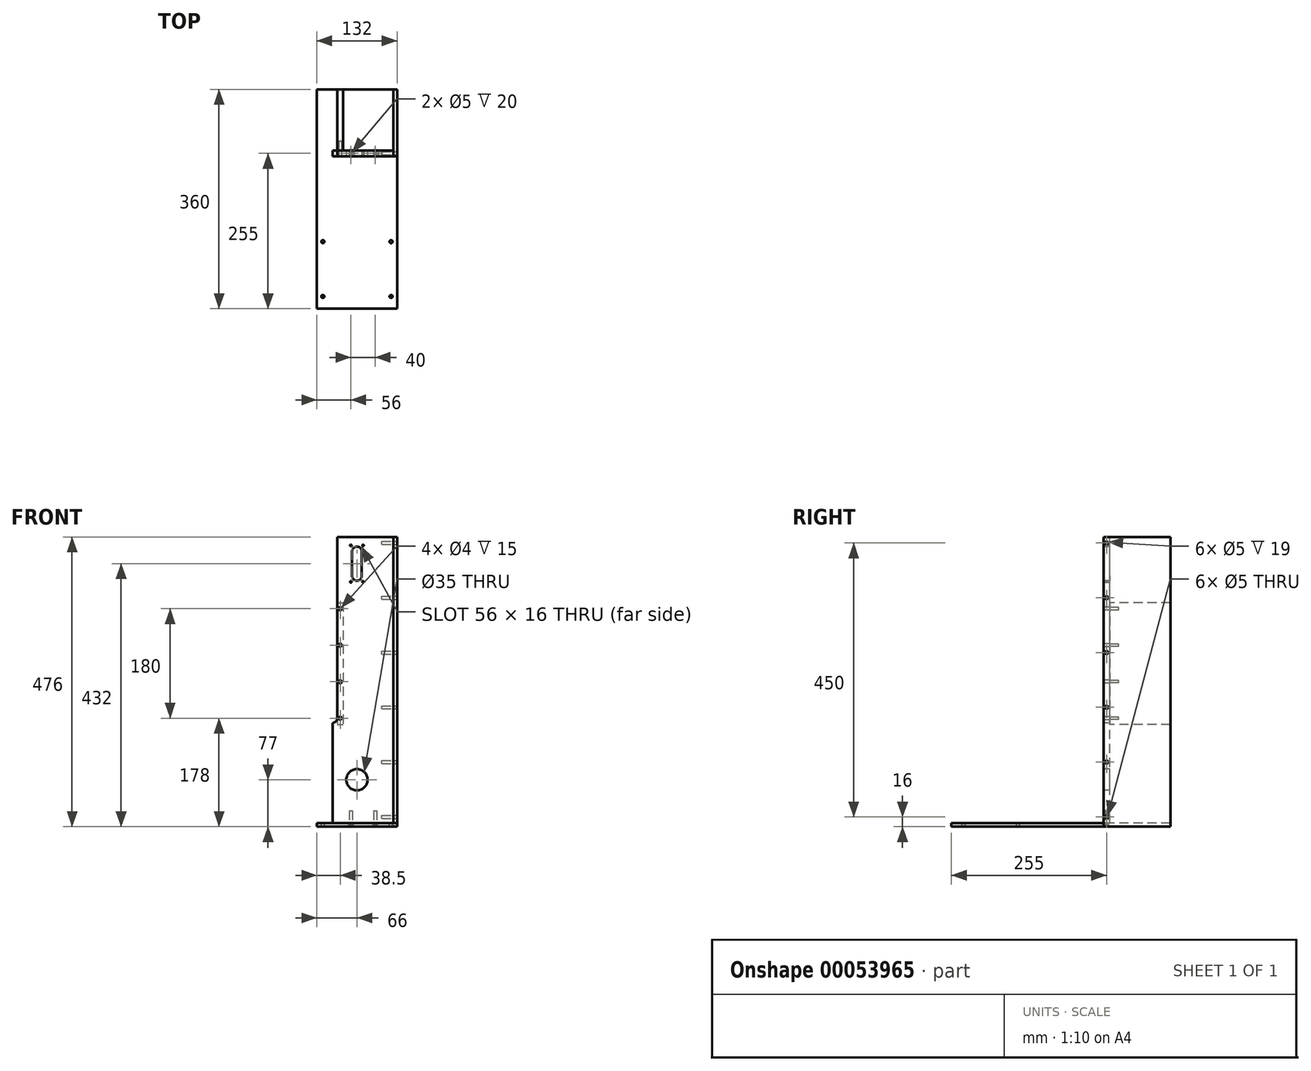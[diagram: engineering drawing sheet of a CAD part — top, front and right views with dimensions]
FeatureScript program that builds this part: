
annotation { "Feature Type Name" : "Feature", "Feature Type Description" : "" }
export const myFeature = defineFeature(function(context is Context, id is Id, definition is map)
    precondition{}
    {
        {
            var Q0;
            Q0=qCreatedBy(makeId("Front.planeOp"),FACE);
            var sketch = newSketch(context, id + "F0", { "sketchPlane" : qUnion([Q0])});
            skLineSegment(sketch, "E0.rect.bottom", {"start": v(50, -235) * mm, "end": v(-50, -235) * mm});
            skLineSegment(sketch, "E0.rect.top", {"start": v(50, 235) * mm, "end": v(-50, 235) * mm});
            skLineSegment(sketch, "E0.rect.left", {"start": v(50, -235) * mm, "end": v(50, 235) * mm});
            skLineSegment(sketch, "E0.rect.right", {"start": v(-50, -235) * mm, "end": v(-50, 235) * mm});
            skPoint(sketch, "E0.rect.middle", {"position": v(0, 0) * mm});
            skSolve(sketch);
        }
        {
            var Q0;
            Q0 = qSketchRegion(id + "F0", true);
            extrude(context, id + "F1", {"entities" : qUnion([Q0]), "depth" : 10 * mm});
        }
        {
            var Q0;
            Q0=makeQuery(id+"F1.opExtrude","CAP_FACE",FACE,{"disambiguationData":[OSD([sQuery(id+"F0.wireOp",EDGE,"E0.rect.bottom"),sQuery(id+"F0.wireOp",EDGE,"E0.rect.top"),sQuery(id+"F0.wireOp",EDGE,"E0.rect.left"),sQuery(id+"F0.wireOp",EDGE,"E0.rect.right")])],"isStart":false});
            var sketch = newSketch(context, id + "F2", { "sketchPlane" : qUnion([Q0])});
            skLineSegment(sketch, "E1", {"start": v(-10, -235) * mm, "end": v(-10, 235) * mm, "construction": true});
            skPoint(sketch, "E2", {"position": v(-10, -164) * mm});
            skPoint(sketch, "E3", {"position": v(-10, 191) * mm});
            skCircle(sketch, "E4", {"center": v(-10, -164) * mm, "radius": 17.5 * mm});
            skLineSegment(sketch, "E5.rect.bottom", {"start": v(-18, 171) * mm, "end": v(-2, 171) * mm});
            skLineSegment(sketch, "E5.rect.top", {"start": v(-18, 211) * mm, "end": v(-2, 211) * mm});
            skLineSegment(sketch, "E5.rect.left", {"start": v(-18, 171) * mm, "end": v(-18, 211) * mm});
            skLineSegment(sketch, "E5.rect.right", {"start": v(-2, 171) * mm, "end": v(-2, 211) * mm});
            skArc(sketch, "E6", {"start": v(-2, 211) * mm, "mid": v(-10, 219) * mm, "end": v(-18, 211) * mm});
            skArc(sketch, "E7", {"start": v(-18, 171) * mm, "mid": v(-10, 163) * mm, "end": v(-2, 171) * mm});
            skLineSegment(sketch, "E8", {"start": v(-10, -164) * mm, "end": v(50, -164) * mm, "construction": true});
            skLineSegment(sketch, "E9", {"start": v(0, 221) * mm, "end": v(0, 191) * mm, "construction": true});
            skCircle(sketch, "E10", {"center": v(0, 221) * mm, "radius": 1.25 * mm});
            skLineSegment(sketch, "E11", {"start": v(-50, 191) * mm, "end": v(50, 191) * mm, "construction": true});
            skPoint(sketch, "E11.startSnap0", {"position": v(-18, 191) * mm});
            skCircle(sketch, "E12.MirrorC", {"center": v(0, 161) * mm, "radius": 1.25 * mm});
            skCircle(sketch, "E13.MirrorC", {"center": v(-20, 221) * mm, "radius": 1.25 * mm});
            skCircle(sketch, "E14.MirrorC", {"center": v(-20, 161) * mm, "radius": 1.25 * mm});
            skSolve(sketch);
        }
        {
            var Q0;
            Q0 = qSketchRegion(id + "F2", true);
            extrude(context, id + "F3", {"entities" : qUnion([Q0]), "operationType" : NewBodyOperationType.REMOVE, "oppositeDirection" : true, "depth" : 25 * mm});
        }
        {
            var Q0;
            Q0=makeQuery(id+"F1.opExtrude","CAP_FACE",FACE,{"disambiguationData":[OSD([sQuery(id+"F0.wireOp",EDGE,"E0.rect.bottom"),sQuery(id+"F0.wireOp",EDGE,"E0.rect.top"),sQuery(id+"F0.wireOp",EDGE,"E0.rect.left"),sQuery(id+"F0.wireOp",EDGE,"E0.rect.right")])],"isStart":false});
            var sketch = newSketch(context, id + "F4", { "sketchPlane" : qUnion([Q0])});
            skPoint(sketch, "E15", {"position": v(-10, -63) * mm});
            skLineSegment(sketch, "E16", {"start": v(22.5, -63) * mm, "end": v(-42.5, -63) * mm, "construction": true});
            skLineSegment(sketch, "E17", {"start": v(-42.5, -63) * mm, "end": v(-42.5, 235) * mm});
            skLineSegment(sketch, "E18", {"start": v(-42.5, -63) * mm, "end": v(-50, -63) * mm, "construction": true});
            skArc(sketch, "E19", {"start": v(-42.5, -63) * mm, "mid": v(-44.7, -68.3) * mm, "end": v(-50, -70.5) * mm});
            skLineSegment(sketch, "E20", {"start": v(-10, 211) * mm, "end": v(-10, -164) * mm, "construction": true});
            skSolve(sketch);
        }
        {
            var Q0;
            Q0 = qSketchRegion(id + "F4", true);
            var Q1;
            {var subQ0=sQuery(id+"F4.wireOp",EDGE,"E17");Q1=makeQuery(id+"F4.imprint","IMPRINT",FACE,{"disambiguationData":[TD([[makeQuery(id+"F4.imprint","IMPRINT",EDGE,{"derivedFrom":subQ0}),1.0]])]});}
            extrude(context, id + "F5", {"entities" : qUnion([Q0, Q1]), "operationType" : NewBodyOperationType.REMOVE, "oppositeDirection" : true, "depth" : 25 * mm});
        }
        {
            var Q0;
            Q0=makeQuery(id+"F1.opExtrude","CAP_FACE",FACE,{"disambiguationData":[OSD([sQuery(id+"F0.wireOp",EDGE,"E0.rect.bottom"),sQuery(id+"F0.wireOp",EDGE,"E0.rect.top"),sQuery(id+"F0.wireOp",EDGE,"E0.rect.left"),sQuery(id+"F0.wireOp",EDGE,"E0.rect.right")])],"isStart":false});
            var sketch = newSketch(context, id + "F6", { "sketchPlane" : qUnion([Q0])});
            skLineSegment(sketch, "E21", {"start": v(-42.5, -63) * mm, "end": v(-37.5, -63) * mm, "construction": true});
            skLineSegment(sketch, "E22", {"start": v(-37.5, -63) * mm, "end": v(-37.5, 235) * mm, "construction": true});
            skCircle(sketch, "E23", {"center": v(-37.5, -63) * mm, "radius": 2.5 * mm});
            skCircle(sketch, "E24", {"center": v(-10, 171) * mm, "radius": 36.88 * mm, "construction": true});
            skCircle(sketch, "E25.1.0.0", {"center": v(-37.5, -3) * mm, "radius": 2.5 * mm});
            skLineSegment(sketch, "E25.direction1", {"start": v(-37.5, -63) * mm, "end": v(-37.5, -3) * mm, "construction": true});
            skCircle(sketch, "E26.0.2.0", {"center": v(-37.5, 57) * mm, "radius": 2.5 * mm});
            skCircle(sketch, "E26.0.3.0", {"center": v(-37.5, 117) * mm, "radius": 2.5 * mm});
            skSolve(sketch);
        }
        {
            var Q0;
            Q0 = qSketchRegion(id + "F6", true);
            extrude(context, id + "F7", {"entities" : qUnion([Q0]), "operationType" : NewBodyOperationType.REMOVE, "oppositeDirection" : true, "depth" : 25 * mm});
        }
        {
            var Q0;
            Q0=makeQuery(id+"F1.opExtrude","CAP_FACE",FACE,{"disambiguationData":[OSD([sQuery(id+"F0.wireOp",EDGE,"E0.rect.bottom"),sQuery(id+"F0.wireOp",EDGE,"E0.rect.top"),sQuery(id+"F0.wireOp",EDGE,"E0.rect.left"),sQuery(id+"F0.wireOp",EDGE,"E0.rect.right")])],"isStart":true});
            var sketch = newSketch(context, id + "F8", { "sketchPlane" : qUnion([Q0])});
            skLineSegment(sketch, "E27", {"start": v(37.5, -63) * mm, "end": v(37.5, 117) * mm, "construction": true});
            skLineSegment(sketch, "E28", {"start": v(37.5, 117) * mm, "end": v(37.5, 127) * mm, "construction": true});
            skLineSegment(sketch, "E29", {"start": v(37.5, -63) * mm, "end": v(37.5, -73) * mm, "construction": true});
            skLineSegment(sketch, "E30.rect.bottom", {"start": v(42.5, 127) * mm, "end": v(32.5, 127) * mm});
            skLineSegment(sketch, "E30.rect.top", {"start": v(42.5, -73) * mm, "end": v(32.5, -73) * mm});
            skLineSegment(sketch, "E30.rect.left", {"start": v(42.5, 127) * mm, "end": v(42.5, -73) * mm});
            skLineSegment(sketch, "E30.rect.right", {"start": v(32.5, 127) * mm, "end": v(32.5, -73) * mm});
            skPoint(sketch, "E30.rect.middle", {"position": v(37.5, 27) * mm});
            skSolve(sketch);
        }
        {
            var Q0;
            Q0 = qSketchRegion(id + "F8", true);
            extrude(context, id + "F9", {"entities" : qUnion([Q0]), "depth" : 100 * mm});
        }
        {
            var Q0;
            Q0=makeQuery(id+"F9.opExtrude","CAP_FACE",FACE,{"disambiguationData":[OSD([sQuery(id+"F8.wireOp",EDGE,"E30.rect.bottom"),sQuery(id+"F8.wireOp",EDGE,"E30.rect.top"),sQuery(id+"F8.wireOp",EDGE,"E30.rect.left"),sQuery(id+"F8.wireOp",EDGE,"E30.rect.right")])],"isStart":true});
            var sketch = newSketch(context, id + "F10", { "sketchPlane" : qUnion([Q0])});
            skLineSegment(sketch, "E31", {"start": v(-37.5, 127) * mm, "end": v(-37.5, 117) * mm, "construction": true});
            skPoint(sketch, "E32", {"position": v(-37.5, 117) * mm});
            skCircle(sketch, "E33", {"center": v(-37.5, 117) * mm, "radius": 2 * mm});
            skCircle(sketch, "E34.1.0.0", {"center": v(-37.5, 57) * mm, "radius": 2 * mm});
            skCircle(sketch, "E34.2.0.0", {"center": v(-37.5, -3) * mm, "radius": 2 * mm});
            skCircle(sketch, "E34.3.0.0", {"center": v(-37.5, -63) * mm, "radius": 2 * mm});
            skLineSegment(sketch, "E34.direction1", {"start": v(-37.5, 117) * mm, "end": v(-37.5, 57) * mm, "construction": true});
            skLineSegment(sketch, "E35", {"start": v(-37.5, 127) * mm, "end": v(-37.5, -73) * mm, "construction": true});
            skSolve(sketch);
        }
        {
            var Q0;
            Q0 = qSketchRegion(id + "F10", true);
            extrude(context, id + "F11", {"entities" : qUnion([Q0]), "operationType" : NewBodyOperationType.REMOVE, "oppositeDirection" : true, "depth" : 15 * mm});
        }
        {
            var Q0;
            Q0=makeQuery(id+"F1.opExtrude","SWEPT_FACE",FACE,{"disambiguationData":[OSD([sQuery(id+"F0.wireOp",EDGE,"E0.rect.bottom")])]});
            var sketch = newSketch(context, id + "F12", { "sketchPlane" : qUnion([Q0])});
            skLineSegment(sketch, "E36", {"start": v(-50, 5) * mm, "end": v(50, 5) * mm, "construction": true});
            skPoint(sketch, "E37", {"position": v(-20, 5) * mm});
            skPoint(sketch, "E38", {"position": v(20, 5) * mm});
            skCircle(sketch, "E39", {"center": v(-20, 5) * mm, "radius": 2.5 * mm});
            skCircle(sketch, "E40", {"center": v(20, 5) * mm, "radius": 2.5 * mm});
            skPoint(sketch, "E41", {"position": v(0, 5) * mm});
            skSolve(sketch);
        }
        {
            var Q0;
            Q0 = qSketchRegion(id + "F12", true);
            extrude(context, id + "F13", {"entities" : qUnion([Q0]), "operationType" : NewBodyOperationType.REMOVE, "oppositeDirection" : true, "depth" : 20 * mm});
        }
        {
            var Q0;
            Q0=makeQuery(id+"F1.opExtrude","SWEPT_FACE",FACE,{"disambiguationData":[OSD([sQuery(id+"F0.wireOp",EDGE,"E0.rect.bottom")])]});
            var sketch = newSketch(context, id + "F14", { "sketchPlane" : qUnion([Q0])});
            skLineSegment(sketch, "E42", {"start": v(-20, 5) * mm, "end": v(20, 5) * mm, "construction": true});
            skLineSegment(sketch, "E43", {"start": v(-76, 0) * mm, "end": v(-76, -100) * mm, "construction": true});
            skLineSegment(sketch, "E44", {"start": v(-76, 10) * mm, "end": v(-76, 260) * mm, "construction": true});
            skLineSegment(sketch, "E45", {"start": v(-76, -100) * mm, "end": v(56, -100) * mm, "construction": true});
            skLineSegment(sketch, "E46.bottom", {"start": v(-76, 260) * mm, "end": v(56, 260) * mm});
            skLineSegment(sketch, "E46.top", {"start": v(-76, -100) * mm, "end": v(56, -100) * mm});
            skLineSegment(sketch, "E46.left", {"start": v(-76, 260) * mm, "end": v(-76, -100) * mm});
            skLineSegment(sketch, "E46.right", {"start": v(56, 260) * mm, "end": v(56, -100) * mm});
            skSolve(sketch);
        }
        {
            var Q0;
            Q0 = qSketchRegion(id + "F14", true);
            var Q1;
            {var subQ0=sQuery(id+"F14.wireOp",EDGE,"E46.bottom");Q1=makeQuery(id+"F14.imprint","IMPRINT",FACE,{"disambiguationData":[TD([[makeQuery(id+"F14.imprint","IMPRINT",EDGE,{"derivedFrom":subQ0}),-1.0]])]});}
            extrude(context, id + "F15", {"entities" : qUnion([Q0, Q1]), "depth" : 6 * mm});
        }
        {
            var Q0;
            Q0=makeQuery(id+"F15.opExtrude","CAP_FACE",FACE,{"disambiguationData":[OSD([sQuery(id+"F14.wireOp",EDGE,"E46.bottom"),sQuery(id+"F14.wireOp",EDGE,"E46.top"),sQuery(id+"F14.wireOp",EDGE,"E46.left"),sQuery(id+"F14.wireOp",EDGE,"E46.right")])],"isStart":true});
            var sketch = newSketch(context, id + "F16", { "sketchPlane" : qUnion([Q0])});
            skLineSegment(sketch, "E47", {"start": v(56, 0) * mm, "end": v(-76, 0) * mm, "construction": true});
            skLineSegment(sketch, "E48", {"start": v(-20, 0) * mm, "end": v(-20, -5) * mm, "construction": true});
            skLineSegment(sketch, "E49", {"start": v(20, 0) * mm, "end": v(20, -5) * mm, "construction": true});
            skCircle(sketch, "E50", {"center": v(20, -5) * mm, "radius": 3 * mm});
            skCircle(sketch, "E51", {"center": v(-20, -5) * mm, "radius": 3 * mm});
            skSolve(sketch);
        }
        {
            var Q0;
            Q0 = qSketchRegion(id + "F16", true);
            extrude(context, id + "F17", {"entities" : qUnion([Q0]), "operationType" : NewBodyOperationType.REMOVE, "oppositeDirection" : true, "depth" : 25 * mm});
        }
        {
            var Q0;
            Q0=makeQuery(id+"F17.boolean.opBoolean","INTERSECT",EDGE,{"derivedFrom":[makeQuery(id+"F15.opExtrude","CAP_FACE",FACE,{"disambiguationData":[OSD([sQuery(id+"F14.wireOp",EDGE,"E46.bottom"),sQuery(id+"F14.wireOp",EDGE,"E46.top"),sQuery(id+"F14.wireOp",EDGE,"E46.left"),sQuery(id+"F14.wireOp",EDGE,"E46.right")])],"isStart":false}),makeQuery(id+"F17.opExtrude","SWEPT_FACE",FACE,{"disambiguationData":[OSD([sQuery(id+"F16.wireOp",EDGE,"E51")])]})]});
            var Q1;
            Q1=makeQuery(id+"F17.boolean.opBoolean","INTERSECT",EDGE,{"derivedFrom":[makeQuery(id+"F15.opExtrude","CAP_FACE",FACE,{"disambiguationData":[OSD([sQuery(id+"F14.wireOp",EDGE,"E46.bottom"),sQuery(id+"F14.wireOp",EDGE,"E46.top"),sQuery(id+"F14.wireOp",EDGE,"E46.left"),sQuery(id+"F14.wireOp",EDGE,"E46.right")])],"isStart":false}),makeQuery(id+"F17.opExtrude","SWEPT_FACE",FACE,{"disambiguationData":[OSD([sQuery(id+"F16.wireOp",EDGE,"E50")])]})]});
            chamfer(context, id + "F18", {"entities" : qUnion([Q0, Q1]), "chamferType" : ChamferType.OFFSET_ANGLE, "width" : 3 * mm, "oppositeDirection" : false, "angle" : 45 * degree, "tangentPropagation" : true});
        }
        {
            var Q0;
            Q0=makeQuery(id+"F15.opExtrude","CAP_FACE",FACE,{"disambiguationData":[OSD([sQuery(id+"F14.wireOp",EDGE,"E46.bottom"),sQuery(id+"F14.wireOp",EDGE,"E46.top"),sQuery(id+"F14.wireOp",EDGE,"E46.left"),sQuery(id+"F14.wireOp",EDGE,"E46.right")])],"isStart":true});
            var sketch = newSketch(context, id + "F19", { "sketchPlane" : qUnion([Q0])});
            skLineSegment(sketch, "E52", {"start": v(-76, -150) * mm, "end": v(56, -150) * mm, "construction": true});
            skLineSegment(sketch, "E53", {"start": v(-76, -240) * mm, "end": v(56, -240) * mm, "construction": true});
            skPoint(sketch, "E54", {"position": v(-10, -240) * mm});
            skPoint(sketch, "E55", {"position": v(-10, -150) * mm});
            skPoint(sketch, "E56", {"position": v(-66, -240) * mm});
            skPoint(sketch, "E57", {"position": v(-66, -150) * mm});
            skLineSegment(sketch, "E58", {"start": v(-10, -150) * mm, "end": v(-10, -260) * mm, "construction": true});
            skPoint(sketch, "E59.MirrorP", {"position": v(46, -150) * mm});
            skPoint(sketch, "E60.MirrorP", {"position": v(46, -240) * mm});
            skCircle(sketch, "E61", {"center": v(-66, -240) * mm, "radius": 2.5 * mm});
            skCircle(sketch, "E62", {"center": v(-66, -150) * mm, "radius": 2.5 * mm});
            skCircle(sketch, "E63.MirrorC", {"center": v(46, -150) * mm, "radius": 2.5 * mm});
            skCircle(sketch, "E64.MirrorC", {"center": v(46, -240) * mm, "radius": 2.5 * mm});
            skSolve(sketch);
        }
        {
            var Q0;
            Q0 = qSketchRegion(id + "F19", true);
            extrude(context, id + "F20", {"entities" : qUnion([Q0]), "operationType" : NewBodyOperationType.REMOVE, "oppositeDirection" : true, "depth" : 25 * mm});
        }
        {
            var Q0;
            Q0=makeQuery(id+"F15.opExtrude","CAP_FACE",FACE,{"disambiguationData":[OSD([sQuery(id+"F14.wireOp",EDGE,"E46.bottom"),sQuery(id+"F14.wireOp",EDGE,"E46.top"),sQuery(id+"F14.wireOp",EDGE,"E46.left"),sQuery(id+"F14.wireOp",EDGE,"E46.right")])],"isStart":true});
            var sketch = newSketch(context, id + "F21", { "sketchPlane" : qUnion([Q0])});
            skLineSegment(sketch, "E65.bottom", {"start": v(50, 100) * mm, "end": v(56, 100) * mm});
            skLineSegment(sketch, "E65.top", {"start": v(50, -10) * mm, "end": v(56, -10) * mm});
            skLineSegment(sketch, "E65.left", {"start": v(50, 100) * mm, "end": v(50, -10) * mm});
            skLineSegment(sketch, "E65.right", {"start": v(56, 100) * mm, "end": v(56, -10) * mm});
            skSolve(sketch);
        }
        {
            var Q0;
            Q0 = qSketchRegion(id + "F21", true);
            extrude(context, id + "F22", {"entities" : qUnion([Q0]), "operationType" : NewBodyOperationType.REMOVE, "oppositeDirection" : true, "depth" : 25 * mm});
        }
        {
            var Q0;
            Q0=makeQuery(id+"F1.opExtrude","SWEPT_FACE",FACE,{"disambiguationData":[OSD([sQuery(id+"F0.wireOp",EDGE,"E0.rect.left")])]});
            var sketch = newSketch(context, id + "F23", { "sketchPlane" : qUnion([Q0])});
            skLineSegment(sketch, "E66.bottom", {"start": v(-10, -241) * mm, "end": v(100, -241) * mm});
            skLineSegment(sketch, "E66.top", {"start": v(-10, 235) * mm, "end": v(100, 235) * mm});
            skLineSegment(sketch, "E66.left", {"start": v(-10, -235) * mm, "end": v(-10, 235) * mm});
            skLineSegment(sketch, "E66.right", {"start": v(100, -241) * mm, "end": v(100, 235) * mm});
            skPoint(sketch, "E67", {"position": v(-10, -241) * mm});
            skLineSegment(sketch, "E68", {"start": v(-10, -241) * mm, "end": v(-10, -235) * mm});
            skSolve(sketch);
        }
        {
            var Q0;
            {var subQ2=sQuery(id+"F23.wireOp",EDGE,"E66.right");Q0=makeQuery(id+"F23.imprint","IMPRINT",FACE,{"disambiguationData":[TD([[makeQuery(id+"F23.imprint","IMPRINT",EDGE,{"derivedFrom":subQ2}),1.0]])]});}
            var Q1;
            {var subQ2=sQuery(id+"F23.wireOp",EDGE,"E66.left");Q1=makeQuery(id+"F23.imprint","IMPRINT",FACE,{"disambiguationData":[TD([[makeQuery(id+"F23.imprint","IMPRINT",EDGE,{"derivedFrom":subQ2}),-1.0]])]});}
            extrude(context, id + "F24", {"entities" : qUnion([Q0, Q1]), "depth" : 6 * mm});
        }
        {
            var Q0;
            Q0=makeQuery(id+"F24.opExtrude","CAP_FACE",FACE,{"disambiguationData":[OSD([sQuery(id+"F23.wireOp",EDGE,"E66.bottom"),sQuery(id+"F23.wireOp",EDGE,"E66.top"),sQuery(id+"F23.wireOp",EDGE,"E66.left"),sQuery(id+"F23.wireOp",EDGE,"E66.right"),sQuery(id+"F23.wireOp",EDGE,"E68")])],"isStart":false});
            var sketch = newSketch(context, id + "F25", { "sketchPlane" : qUnion([Q0])});
            skLineSegment(sketch, "E69", {"start": v(-5, -241) * mm, "end": v(-5, 235) * mm, "construction": true});
            skCircle(sketch, "E70", {"center": v(-5, 225) * mm, "radius": 2.5 * mm});
            skCircle(sketch, "E71.0.1.0", {"center": v(-5, 135) * mm, "radius": 2.5 * mm});
            skCircle(sketch, "E71.0.2.0", {"center": v(-5, 45) * mm, "radius": 2.5 * mm});
            skCircle(sketch, "E71.0.3.0", {"center": v(-5, -45) * mm, "radius": 2.5 * mm});
            skCircle(sketch, "E71.0.4.0", {"center": v(-5, -135) * mm, "radius": 2.5 * mm});
            skCircle(sketch, "E71.0.5.0", {"center": v(-5, -225) * mm, "radius": 2.5 * mm});
            skLineSegment(sketch, "E71.direction1", {"start": v(-5, 225) * mm, "end": v(20, 225) * mm, "construction": true});
            skLineSegment(sketch, "E71.direction2", {"start": v(-5, 225) * mm, "end": v(-5, 135) * mm, "construction": true});
            skSolve(sketch);
        }
        {
            var Q0;
            Q0 = qSketchRegion(id + "F25", true);
            extrude(context, id + "F26", {"entities" : qUnion([Q0]), "operationType" : NewBodyOperationType.REMOVE, "oppositeDirection" : true, "depth" : 25 * mm});
        }
    });
